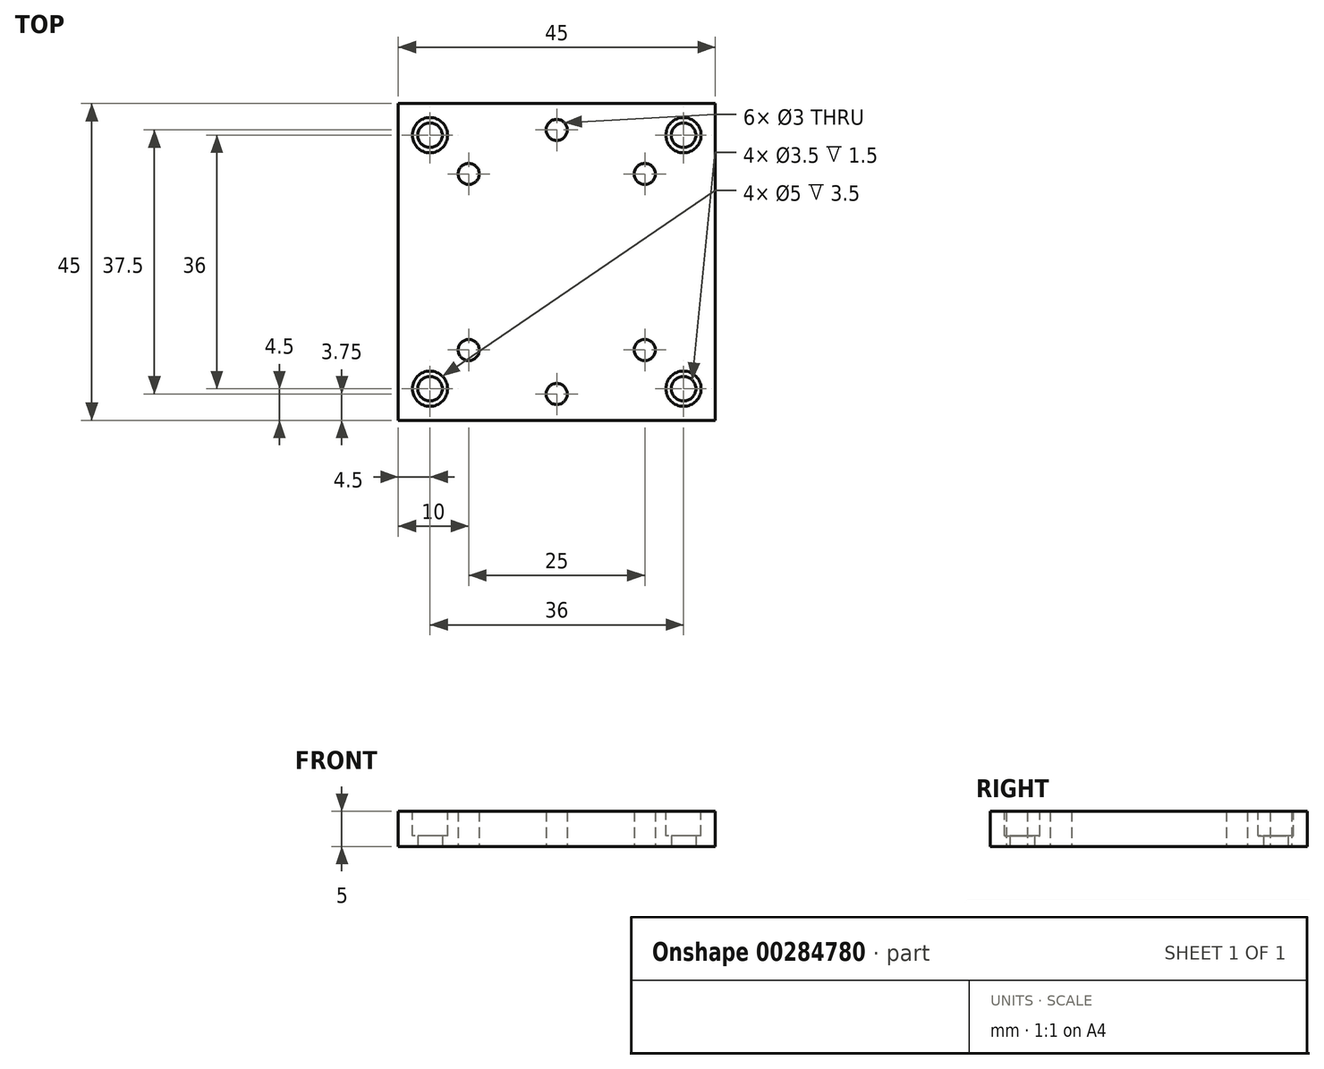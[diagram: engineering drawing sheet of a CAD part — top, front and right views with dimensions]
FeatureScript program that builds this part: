
annotation { "Feature Type Name" : "Feature", "Feature Type Description" : "" }
export const myFeature = defineFeature(function(context is Context, id is Id, definition is map)
    precondition{}
    {
        {
            var Q0;
            Q0=qCreatedBy(makeId("Top.planeOp"),FACE);
            var sketch = newSketch(context, id + "F0", { "sketchPlane" : qUnion([Q0])});
            skLineSegment(sketch, "E0.bottom", {"start": v(-22.5, 22.5) * mm, "end": v(22.5, 22.5) * mm});
            skLineSegment(sketch, "E0.top", {"start": v(-22.5, -22.5) * mm, "end": v(22.5, -22.5) * mm});
            skLineSegment(sketch, "E0.left", {"start": v(-22.5, 22.5) * mm, "end": v(-22.5, -22.5) * mm});
            skLineSegment(sketch, "E0.right", {"start": v(22.5, 22.5) * mm, "end": v(22.5, -22.5) * mm});
            skCircle(sketch, "E1", {"center": v(-18, 18) * mm, "radius": 1.75 * mm});
            skCircle(sketch, "E2", {"center": v(-18, -18) * mm, "radius": 1.75 * mm});
            skCircle(sketch, "E3", {"center": v(18, -18) * mm, "radius": 1.75 * mm});
            skCircle(sketch, "E4", {"center": v(18, 18) * mm, "radius": 1.75 * mm});
            skCircle(sketch, "E5", {"center": v(-12.5, 12.5) * mm, "radius": 1.5 * mm});
            skCircle(sketch, "E6", {"center": v(12.5, 12.5) * mm, "radius": 1.5 * mm});
            skCircle(sketch, "E7", {"center": v(-12.5, -12.5) * mm, "radius": 1.5 * mm});
            skCircle(sketch, "E8", {"center": v(12.5, -12.5) * mm, "radius": 1.5 * mm});
            skCircle(sketch, "E9", {"center": v(0, 18.75) * mm, "radius": 1.5 * mm});
            skCircle(sketch, "E10", {"center": v(0, -18.75) * mm, "radius": 1.5 * mm});
            skSolve(sketch);
        }
        {
            var Q0;
            Q0 = qSketchRegion(id + "F0", true);
            extrude(context, id + "F1", {"entities" : qUnion([Q0]), "depth" : 5 * mm});
        }
        {
            var Q0;
            Q0=makeQuery(id+"F1.opExtrude","CAP_FACE",FACE,{"disambiguationData":[OSD([sQuery(id+"F0.wireOp",EDGE,"E0.bottom"),sQuery(id+"F0.wireOp",EDGE,"E0.top"),sQuery(id+"F0.wireOp",EDGE,"E0.left"),sQuery(id+"F0.wireOp",EDGE,"E0.right"),sQuery(id+"F0.wireOp",EDGE,"E1"),sQuery(id+"F0.wireOp",EDGE,"E2"),sQuery(id+"F0.wireOp",EDGE,"E3"),sQuery(id+"F0.wireOp",EDGE,"E4"),sQuery(id+"F0.wireOp",EDGE,"E5"),sQuery(id+"F0.wireOp",EDGE,"E6"),sQuery(id+"F0.wireOp",EDGE,"E7"),sQuery(id+"F0.wireOp",EDGE,"E8")])],"isStart":false});
            var sketch = newSketch(context, id + "F2", { "sketchPlane" : qUnion([Q0])});
            skCircle(sketch, "E11", {"center": v(-18, 18) * mm, "radius": 2.5 * mm});
            skCircle(sketch, "E12", {"center": v(-18, -18) * mm, "radius": 2.5 * mm});
            skCircle(sketch, "E13", {"center": v(18, 18) * mm, "radius": 2.5 * mm});
            skCircle(sketch, "E14", {"center": v(18, -18) * mm, "radius": 2.5 * mm});
            skSolve(sketch);
        }
        {
            var Q0;
            Q0 = qSketchRegion(id + "F2", true);
            extrude(context, id + "F3", {"entities" : qUnion([Q0]), "operationType" : NewBodyOperationType.REMOVE, "oppositeDirection" : true, "depth" : 3.5 * mm});
        }
    });
